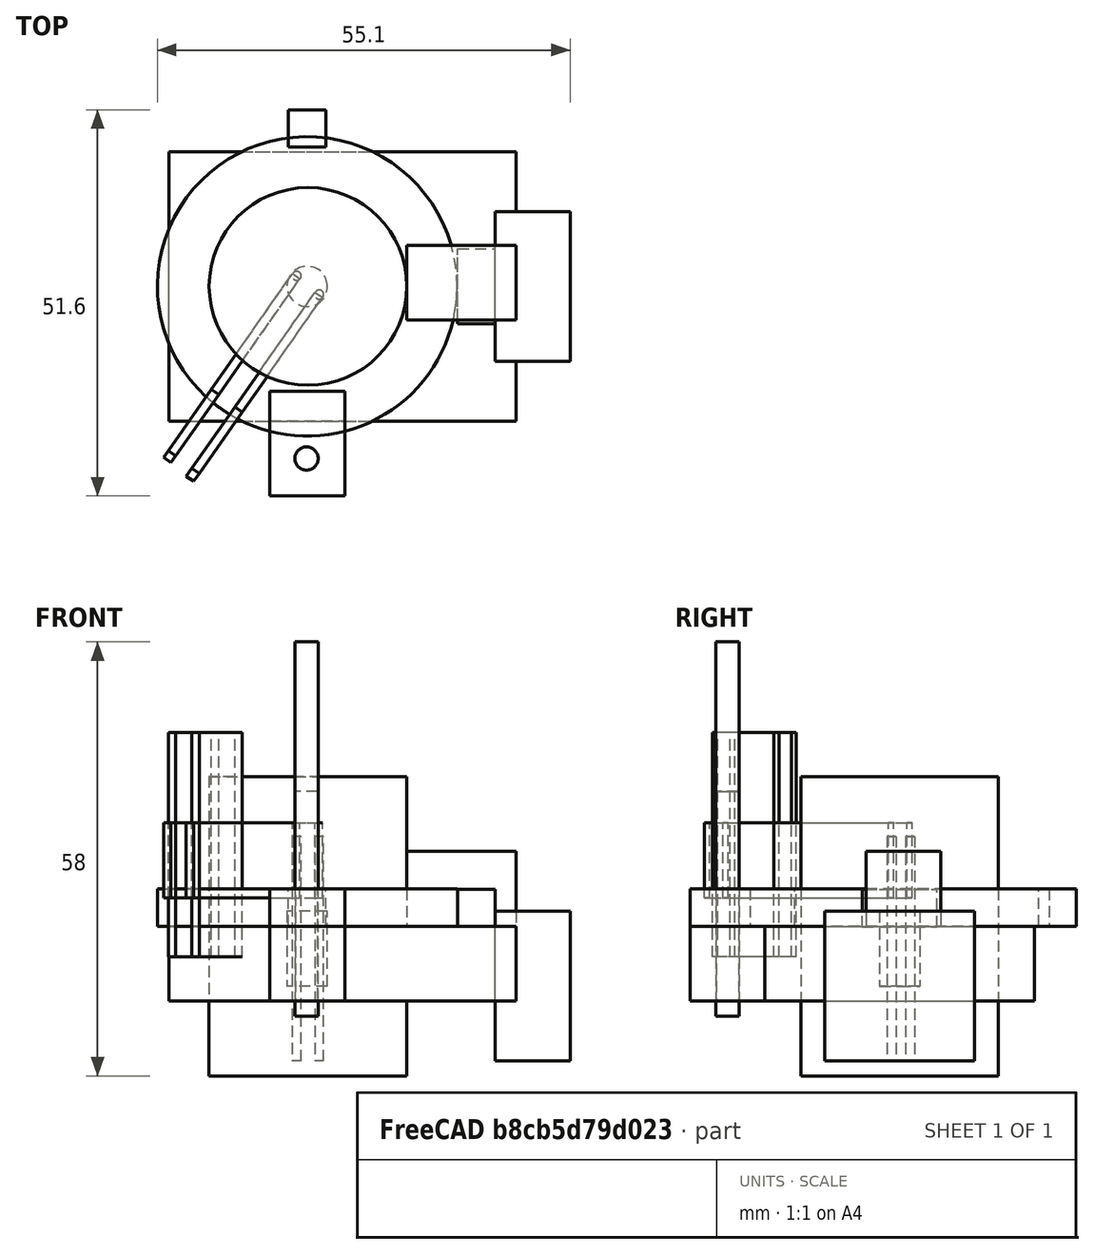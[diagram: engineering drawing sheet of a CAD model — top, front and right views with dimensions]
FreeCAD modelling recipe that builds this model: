
FCSTD DOCUMENT  (FreeCAD 1.0R39319 (Git))
Label: CdSHolder
License: All rights reserved
LicenseURL: https://en.wikipedia.org/wiki/All_rights_reserved
objects: Part::Box×11, Part::Cylinder×7
note: 18 computed .brp shape members not serialized (recipe doc carries the construction recipe); baked Part::Feature solids carry a one-line shape summary decoded from their .brp

FEATURE [Part::Cylinder] Cylinder  label="cardboardBarrelHolder"
  Angle = 360
  AttacherType = Attacher::AttachEngine3D
  FirstAngle = 0
  Height = 40
  Placement = pos=(-1.1,0,-20) rot=(0,0,1;0rad)
  Radius = 13.2
  SecondAngle = 0
FEATURE [Part::Box] Box  label="mainPiece"
  AttacherType = Attacher::AttachEngine3D
  Height = 46.4
  Length = 10
  Placement = pos=(-19.7,-18,-4.4e-15) rot=(0,1,0;1.5708rad)
  Width = 36
FEATURE [Part::Box] Box001  label="Cube001"
  AttacherType = Attacher::AttachEngine3D
  Height = 14.6
  Length = 10
  Placement = pos=(12.1,-4.5,10) rot=(0,1,0;1.5708rad)
  Width = 10
FEATURE [Part::Box] Box002  label="hingePinTab"
  AttacherType = Attacher::AttachEngine3D
  Height = 10
  Length = 10
  Placement = pos=(-6.2,-27.952,-10) rot=(0,0,1;0rad)
  Width = 10
FEATURE [Part::Cylinder] Cylinder001  label="hingeTabHole"
  Angle = 360
  AttacherType = Attacher::AttachEngine3D
  FirstAngle = 0
  Height = 30
  Placement = pos=(-1.3,-23,-12) rot=(0,0,1;0rad)
  Radius = 1.5
  SecondAngle = 0
FEATURE [Part::Cylinder] Cylinder002  label="shutter"
  Angle = 360
  AttacherType = Attacher::AttachEngine3D
  FirstAngle = 0
  Height = 5
  Placement = pos=(-1.2,0,0) rot=(0,0,1;0rad)
  Radius = 20
  SecondAngle = 0
FEATURE [Part::Box] Box003  label="shutterHingeTab"
  AttacherType = Attacher::AttachEngine3D
  Height = 5
  Length = 10
  Placement = pos=(-6.2,-28,0) rot=(0,0,1;0rad)
  Width = 14
FEATURE [Part::Box] Box004  label="swivelStop"
  AttacherType = Attacher::AttachEngine3D
  Height = 5
  Length = 5
  Placement = pos=(18.9,-5,-0.1) rot=(0,0,1;0rad)
  Width = 10
FEATURE [Part::Box] Box005  label="footCutout"
  AttacherType = Attacher::AttachEngine3D
  Height = 20
  Length = 10
  Placement = pos=(23.9,-10,-18) rot=(0,0,1;0rad)
  Width = 20
FEATURE [Part::Cylinder] Cylinder003  label="shutterTabHole"
  Angle = 360
  AttacherType = Attacher::AttachEngine3D
  FirstAngle = 0
  Height = 50
  Placement = pos=(-1.3,-23,-12) rot=(0,0,1;0rad)
  Radius = 1.55
  SecondAngle = 0
FEATURE [Part::Box] Box006  label="shutterMoveTab"
  AttacherType = Attacher::AttachEngine3D
  Height = 5
  Length = 5
  Placement = pos=(-3.7,18.6,0) rot=(0,0,1;0rad)
  Width = 5
FEATURE [Part::Cylinder] Cylinder004  label="CdSDivot"
  Angle = 360
  AttacherType = Attacher::AttachEngine3D
  FirstAngle = 0
  Height = 10
  Placement = pos=(-1.2,0,-8) rot=(0,0,1;0rad)
  Radius = 2.7
  SecondAngle = 0
FEATURE [Part::Cylinder] Cylinder005  label="CdSWire1"
  Angle = 360
  AttacherType = Attacher::AttachEngine3D
  FirstAngle = 0
  Height = 30
  Placement = pos=(0.4,-1.1,-18) rot=(0,0,1;0rad)
  Radius = 0.6
  SecondAngle = 0
FEATURE [Part::Cylinder] Cylinder006  label="CdsWire2"
  Angle = 360
  AttacherType = Attacher::AttachEngine3D
  FirstAngle = 0
  Height = 30
  Placement = pos=(-2.6,1.4,-18) rot=(0,0,1;0rad)
  Radius = 0.6
  SecondAngle = 0
FEATURE [Part::Box] Box007  label="radialTransit1"
  AttacherType = Attacher::AttachEngine3D
  Height = 10
  Length = 1.2
  Placement = pos=(-17.353,-25.3595,3.8) rot=(0,0,1;5.67232rad)
  Width = 30
FEATURE [Part::Box] Box008  label="radialTransit2"
  AttacherType = Attacher::AttachEngine3D
  Height = 10
  Length = 1.2
  Placement = pos=(-20.3756,-22.8768,3.8) rot=(0,0,1;5.67232rad)
  Width = 30
FEATURE [Part::Box] Box009  label="radialTransit3"
  AttacherType = Attacher::AttachEngine3D
  Height = 10
  Length = 1.2
  Placement = pos=(-10.8716,-16.103,-4.1) rot=(-0.913318,0.287968,0.287968;4.62184rad)
  Width = 30
FEATURE [Part::Box] Box010  label="radialTransit4"
  AttacherType = Attacher::AttachEngine3D
  Height = 10
  Length = 1.2
  Placement = pos=(-14.0089,-13.7842,-4.1) rot=(-0.913318,0.287968,0.287968;4.62184rad)
  Width = 30
